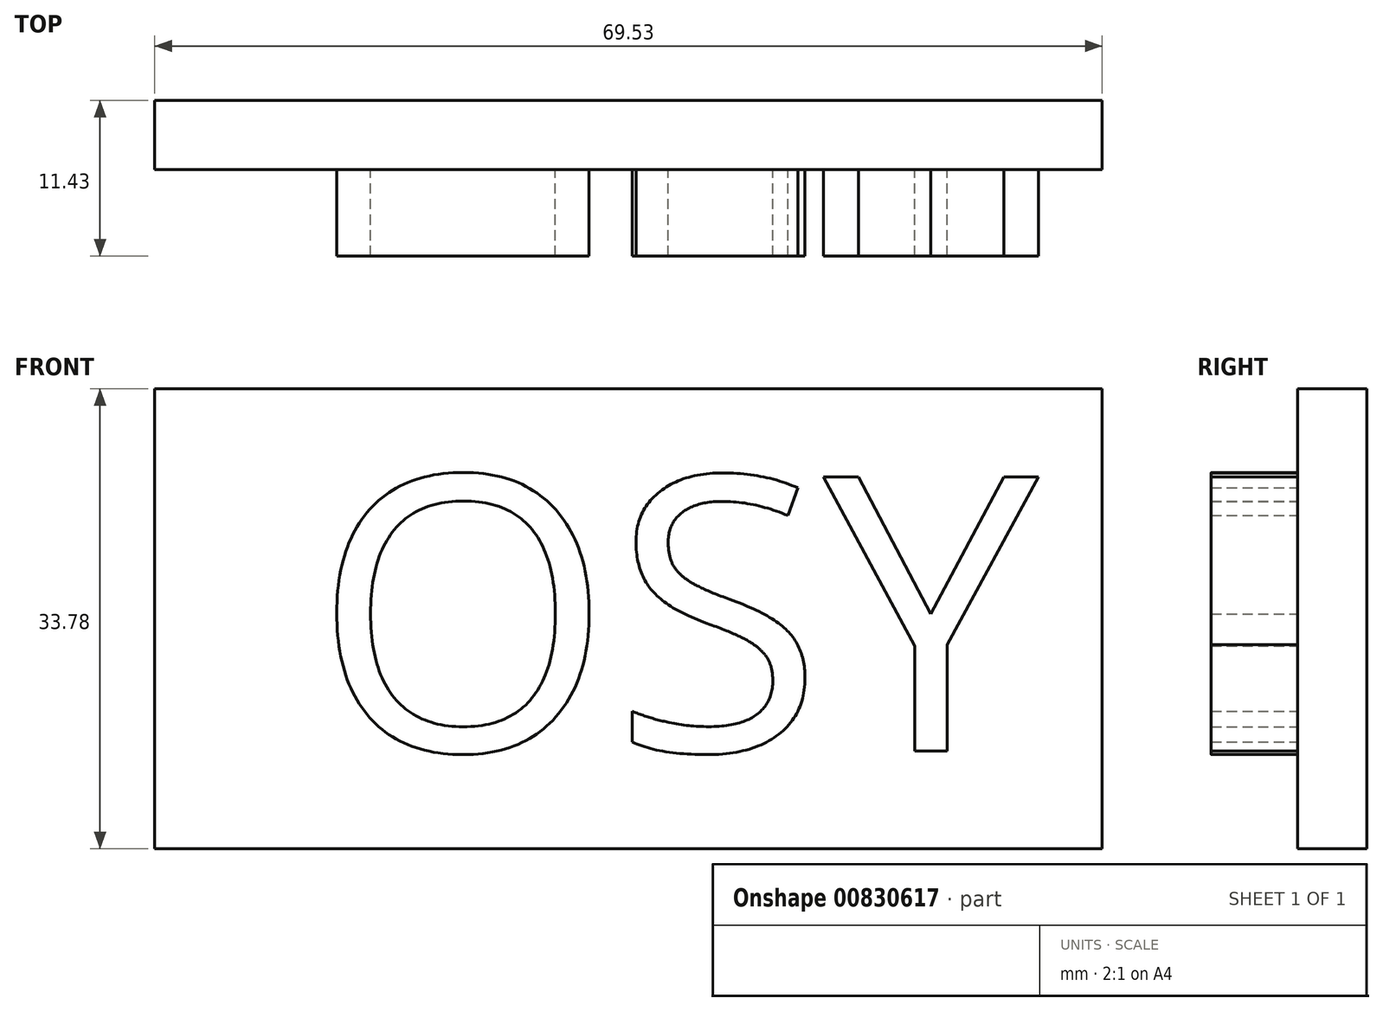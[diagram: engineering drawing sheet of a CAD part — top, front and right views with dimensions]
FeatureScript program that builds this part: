
annotation { "Feature Type Name" : "Feature", "Feature Type Description" : "" }
export const myFeature = defineFeature(function(context is Context, id is Id, definition is map)
    precondition{}
    {
        {
            var Q0;
            Q0=qCreatedBy(makeId("Front.planeOp"),FACE);
            var sketch = newSketch(context, id + "F0", { "sketchPlane" : qUnion([Q0])});
            skLineSegment(sketch, "E0.bottom", {"start": v(0, 0) * mm, "end": v(69.53, 0) * mm});
            skLineSegment(sketch, "E0.top", {"start": v(0, 33.78) * mm, "end": v(69.53, 33.78) * mm});
            skLineSegment(sketch, "E0.left", {"start": v(0, 0) * mm, "end": v(0, 33.78) * mm});
            skLineSegment(sketch, "E0.right", {"start": v(69.53, 0) * mm, "end": v(69.53, 33.78) * mm});
            skSolve(sketch);
        }
        {
            var Q0;
            Q0=makeQuery(id+"F0.imprint","IMPRINT",FACE,{"disambiguationData":[TD([[makeQuery(id+"F0.imprint","IMPRINT",EDGE,{"derivedFrom":sQuery(id+"F0.wireOp",EDGE,"E0.bottom")}),1.0]])]});
            extrude(context, id + "F1", {"entities" : qUnion([Q0]), "depth" : 5.08 * mm, "offsetDistance" : 25.4 * mm});
        }
        {
            var Q0;
            Q0=makeQuery(id+"F1.opExtrude","CAP_FACE",FACE,{"disambiguationData":[OSD([sQuery(id+"F0.wireOp",EDGE,"E0.bottom"),sQuery(id+"F0.wireOp",EDGE,"E0.top"),sQuery(id+"F0.wireOp",EDGE,"E0.left"),sQuery(id+"F0.wireOp",EDGE,"E0.right")])],"isStart":false});
            var sketch = newSketch(context, id + "F2", { "sketchPlane" : qUnion([Q0])});
            skText(sketch, "E1", { "text": "OSY", "fontName": "OpenSans-Regular.ttf"});
            const initialGuessF2  = {"E1": [0.01164, 0.00719, 1, 0, 0.0203]};
            skSetInitialGuess(sketch, initialGuessF2);
            skSolve(sketch);
        }
        {
            var Q0;
            Q0 = qSketchRegion(id + "F2", true);
            extrude(context, id + "F3", {"entities" : qUnion([Q0]), "operationType" : NewBodyOperationType.ADD, "depth" : 6.35 * mm, "offsetDistance" : 25.4 * mm});
        }
    });
